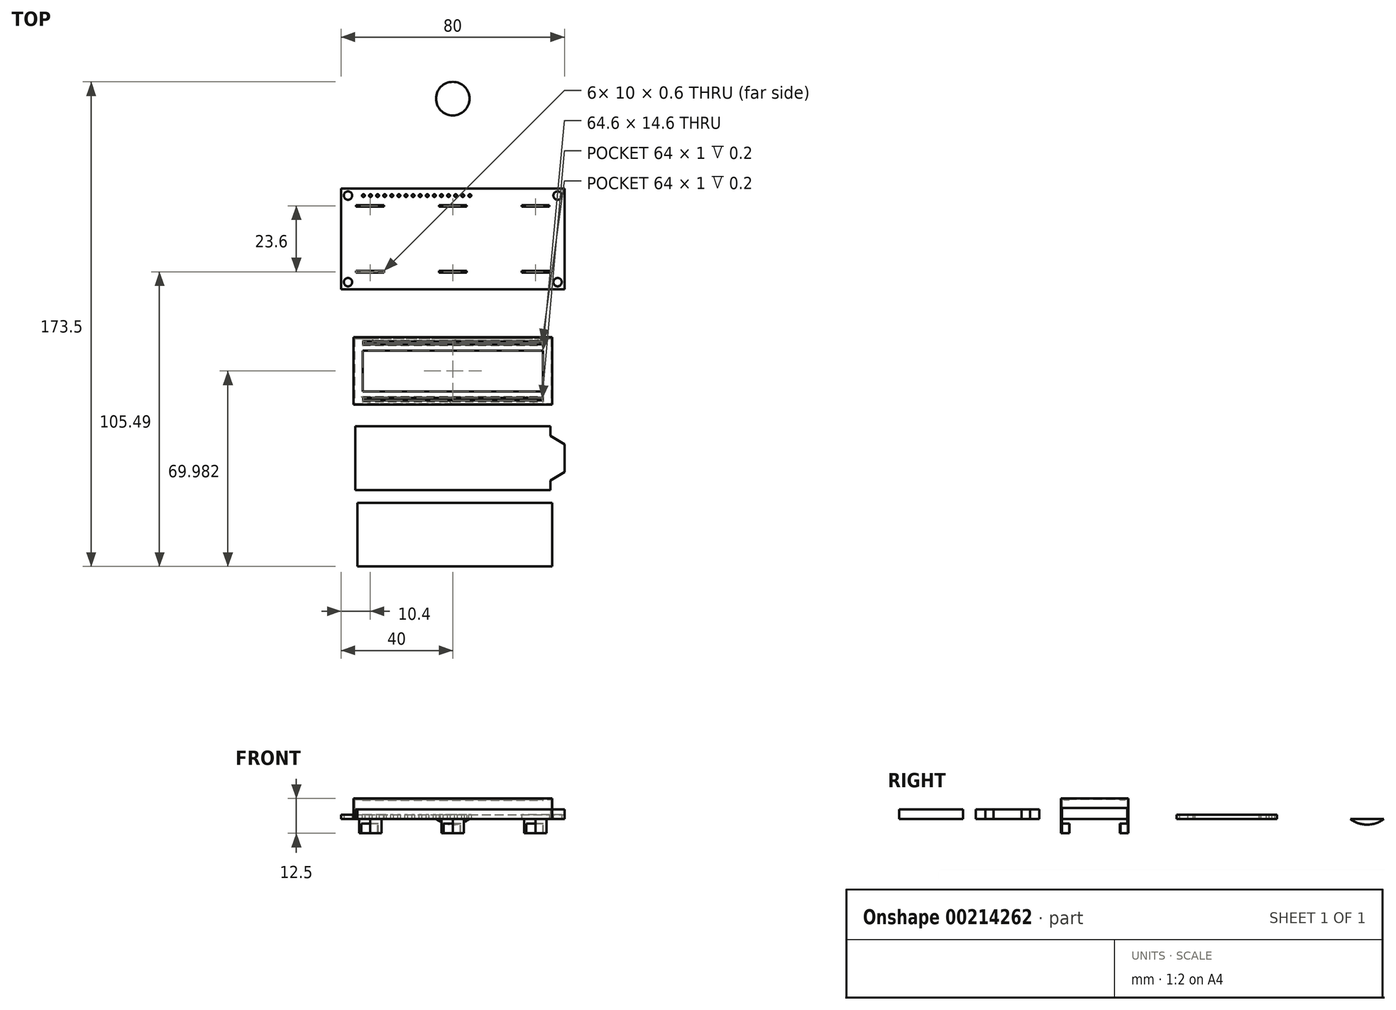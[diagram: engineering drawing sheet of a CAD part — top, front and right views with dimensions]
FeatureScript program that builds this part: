
annotation { "Feature Type Name" : "Feature", "Feature Type Description" : "" }
export const myFeature = defineFeature(function(context is Context, id is Id, definition is map)
    precondition{}
    {
        {
            var Q0;
            Q0=qCreatedBy(makeId("Top.planeOp"),FACE);
            var sketch = newSketch(context, id + "F0", { "sketchPlane" : qUnion([Q0])});
            skLineSegment(sketch, "E0.bottom", {"start": v(-40, 18) * mm, "end": v(40, 18) * mm});
            skLineSegment(sketch, "E0.top", {"start": v(-40, -18) * mm, "end": v(40, -18) * mm});
            skLineSegment(sketch, "E0.left", {"start": v(-40, 18) * mm, "end": v(-40, -18) * mm});
            skLineSegment(sketch, "E0.right", {"start": v(40, 18) * mm, "end": v(40, -18) * mm});
            skSolve(sketch);
        }
        {
            var Q0;
            Q0 = qSketchRegion(id + "F0", true);
            extrude(context, id + "F1", {"entities" : qUnion([Q0]), "depth" : 1.6 * mm});
        }
        {
            var Q0;
            Q0=qCreatedBy(makeId("Top.planeOp"),FACE);
            var sketch = newSketch(context, id + "F2", { "sketchPlane" : qUnion([Q0])});
            skCircle(sketch, "E1", {"center": v(-37.5, 15.5) * mm, "radius": 1.5 * mm});
            skCircle(sketch, "E2", {"center": v(-37.5, -15.5) * mm, "radius": 1.5 * mm});
            skCircle(sketch, "E3", {"center": v(37.5, -15.5) * mm, "radius": 1.5 * mm});
            skCircle(sketch, "E4", {"center": v(37.5, 15.5) * mm, "radius": 1.5 * mm});
            skSolve(sketch);
        }
        {
            var Q0;
            Q0 = qSketchRegion(id + "F2", true);
            extrude(context, id + "F3", {"entities" : qUnion([Q0]), "operationType" : NewBodyOperationType.REMOVE, "endBound" : BoundingType.THROUGH_ALL, "depth" : 25 * mm});
        }
        {
            var Q0;
            Q0=qCreatedBy(makeId("Top.planeOp"),FACE);
            var sketch = newSketch(context, id + "F4", { "sketchPlane" : qUnion([Q0])});
            skCircle(sketch, "E5", {"center": v(-32, 15.5) * mm, "radius": 0.5 * mm});
            skCircle(sketch, "E6.1.0.0", {"center": v(-29.46, 15.5) * mm, "radius": 0.5 * mm});
            skCircle(sketch, "E6.2.0.0", {"center": v(-26.92, 15.5) * mm, "radius": 0.5 * mm});
            skCircle(sketch, "E6.3.0.0", {"center": v(-24.38, 15.5) * mm, "radius": 0.5 * mm});
            skCircle(sketch, "E6.4.0.0", {"center": v(-21.84, 15.5) * mm, "radius": 0.5 * mm});
            skCircle(sketch, "E6.5.0.0", {"center": v(-19.3, 15.5) * mm, "radius": 0.5 * mm});
            skCircle(sketch, "E6.6.0.0", {"center": v(-16.76, 15.5) * mm, "radius": 0.5 * mm});
            skCircle(sketch, "E6.7.0.0", {"center": v(-14.22, 15.5) * mm, "radius": 0.5 * mm});
            skCircle(sketch, "E6.8.0.0", {"center": v(-11.68, 15.5) * mm, "radius": 0.5 * mm});
            skCircle(sketch, "E6.9.0.0", {"center": v(-9.14, 15.5) * mm, "radius": 0.5 * mm});
            skCircle(sketch, "E6.10.0.0", {"center": v(-6.6, 15.5) * mm, "radius": 0.5 * mm});
            skCircle(sketch, "E6.11.0.0", {"center": v(-4.06, 15.5) * mm, "radius": 0.5 * mm});
            skCircle(sketch, "E6.12.0.0", {"center": v(-1.52, 15.5) * mm, "radius": 0.5 * mm});
            skCircle(sketch, "E6.13.0.0", {"center": v(1.02, 15.5) * mm, "radius": 0.5 * mm});
            skCircle(sketch, "E6.14.0.0", {"center": v(3.56, 15.5) * mm, "radius": 0.5 * mm});
            skCircle(sketch, "E6.15.0.0", {"center": v(6.1, 15.5) * mm, "radius": 0.5 * mm});
            skLineSegment(sketch, "E6.direction1", {"start": v(-32, 15.5) * mm, "end": v(-29.46, 15.5) * mm, "construction": true});
            skSolve(sketch);
        }
        {
            var Q0;
            Q0 = qSketchRegion(id + "F4", true);
            extrude(context, id + "F5", {"entities" : qUnion([Q0]), "operationType" : NewBodyOperationType.REMOVE, "endBound" : BoundingType.THROUGH_ALL, "depth" : 25 * mm});
        }
        {
            var Q0;
            Q0=qCreatedBy(makeId("Top.planeOp"),FACE);
            var sketch = newSketch(context, id + "F6", { "sketchPlane" : qUnion([Q0])});
            skLineSegment(sketch, "E7.bottom", {"start": v(-34.6, 12.1) * mm, "end": v(-24.6, 12.1) * mm});
            skLineSegment(sketch, "E7.top", {"start": v(-34.6, 11.5) * mm, "end": v(-24.6, 11.5) * mm});
            skLineSegment(sketch, "E7.left", {"start": v(-34.6, 12.1) * mm, "end": v(-34.6, 11.5) * mm});
            skLineSegment(sketch, "E7.right", {"start": v(-24.6, 12.1) * mm, "end": v(-24.6, 11.5) * mm});
            skLineSegment(sketch, "E8.bottom", {"start": v(-5, 12.1) * mm, "end": v(5, 12.1) * mm});
            skLineSegment(sketch, "E8.top", {"start": v(-5, 11.5) * mm, "end": v(5, 11.5) * mm});
            skLineSegment(sketch, "E8.left", {"start": v(-5, 12.1) * mm, "end": v(-5, 11.5) * mm});
            skLineSegment(sketch, "E8.right", {"start": v(5, 12.1) * mm, "end": v(5, 11.5) * mm});
            skLineSegment(sketch, "E9.bottom", {"start": v(24.6, 12.1) * mm, "end": v(34.6, 12.1) * mm});
            skLineSegment(sketch, "E9.top", {"start": v(24.6, 11.5) * mm, "end": v(34.6, 11.5) * mm});
            skLineSegment(sketch, "E9.left", {"start": v(24.6, 12.1) * mm, "end": v(24.6, 11.5) * mm});
            skLineSegment(sketch, "E9.right", {"start": v(34.6, 12.1) * mm, "end": v(34.6, 11.5) * mm});
            skLineSegment(sketch, "E10.bottom", {"start": v(-34.6, -12.1) * mm, "end": v(-24.6, -12.1) * mm});
            skLineSegment(sketch, "E10.top", {"start": v(-34.6, -11.5) * mm, "end": v(-24.6, -11.5) * mm});
            skLineSegment(sketch, "E10.left", {"start": v(-34.6, -11.5) * mm, "end": v(-34.6, -12.1) * mm});
            skLineSegment(sketch, "E10.right", {"start": v(-24.6, -11.5) * mm, "end": v(-24.6, -12.1) * mm});
            skLineSegment(sketch, "E11.bottom", {"start": v(-5, -12.1) * mm, "end": v(5, -12.1) * mm});
            skLineSegment(sketch, "E11.top", {"start": v(-5, -11.5) * mm, "end": v(5, -11.5) * mm});
            skLineSegment(sketch, "E11.left", {"start": v(-5, -11.5) * mm, "end": v(-5, -12.1) * mm});
            skLineSegment(sketch, "E11.right", {"start": v(5, -11.5) * mm, "end": v(5, -12.1) * mm});
            skLineSegment(sketch, "E12.bottom", {"start": v(24.6, -12.1) * mm, "end": v(34.6, -12.1) * mm});
            skLineSegment(sketch, "E12.top", {"start": v(24.6, -11.5) * mm, "end": v(34.6, -11.5) * mm});
            skLineSegment(sketch, "E12.left", {"start": v(24.6, -11.5) * mm, "end": v(24.6, -12.1) * mm});
            skLineSegment(sketch, "E12.right", {"start": v(34.6, -11.5) * mm, "end": v(34.6, -12.1) * mm});
            skSolve(sketch);
        }
        {
            var Q0;
            Q0 = qSketchRegion(id + "F6", true);
            extrude(context, id + "F7", {"entities" : qUnion([Q0]), "operationType" : NewBodyOperationType.REMOVE, "endBound" : BoundingType.THROUGH_ALL, "depth" : 25 * mm});
        }
        {
            var Q0;
            Q0=qCreatedBy(makeId("Top.planeOp"),FACE);
            var sketch = newSketch(context, id + "F8", { "sketchPlane" : qUnion([Q0])});
            skLineSegment(sketch, "E13.bottom", {"start": v(-35.55, -35.26) * mm, "end": v(35.55, -35.26) * mm});
            skLineSegment(sketch, "E13.top", {"start": v(-35.55, -59.36) * mm, "end": v(35.55, -59.36) * mm});
            skLineSegment(sketch, "E13.left", {"start": v(-35.55, -35.26) * mm, "end": v(-35.55, -59.36) * mm});
            skLineSegment(sketch, "E13.right", {"start": v(35.55, -35.26) * mm, "end": v(35.55, -59.36) * mm});
            skSolve(sketch);
        }
        {
            var Q0;
            Q0 = qSketchRegion(id + "F8", true);
            extrude(context, id + "F9", {"entities" : qUnion([Q0]), "depth" : 7.4 * mm});
        }
        {
            var Q0;
            Q0=makeQuery(id+"F9.opExtrude","CAP_FACE",FACE,{"disambiguationData":[OSD([sQuery(id+"F8.wireOp",EDGE,"E13.bottom"),sQuery(id+"F8.wireOp",EDGE,"E13.top"),sQuery(id+"F8.wireOp",EDGE,"E13.left"),sQuery(id+"F8.wireOp",EDGE,"E13.right")])],"isStart":false});
            var sketch = newSketch(context, id + "F10", { "sketchPlane" : qUnion([Q0])});
            skLineSegment(sketch, "E14.bottom", {"start": v(-32, -36.76) * mm, "end": v(32, -36.76) * mm});
            skLineSegment(sketch, "E14.top", {"start": v(-32, -37.76) * mm, "end": v(32, -37.76) * mm});
            skLineSegment(sketch, "E14.left", {"start": v(-32, -36.76) * mm, "end": v(-32, -37.76) * mm});
            skLineSegment(sketch, "E14.right", {"start": v(32, -36.76) * mm, "end": v(32, -37.76) * mm});
            skLineSegment(sketch, "E15.bottom", {"start": v(-32, -56.86) * mm, "end": v(32, -56.86) * mm});
            skLineSegment(sketch, "E15.top", {"start": v(-32, -57.86) * mm, "end": v(32, -57.86) * mm});
            skLineSegment(sketch, "E15.left", {"start": v(-32, -56.86) * mm, "end": v(-32, -57.86) * mm});
            skLineSegment(sketch, "E15.right", {"start": v(32, -56.86) * mm, "end": v(32, -57.86) * mm});
            skSolve(sketch);
        }
        {
            var Q0;
            Q0 = qSketchRegion(id + "F10", true);
            extrude(context, id + "F11", {"entities" : qUnion([Q0]), "operationType" : NewBodyOperationType.REMOVE, "oppositeDirection" : true, "depth" : .2 * mm});
        }
        {
            var Q0;
            Q0=makeQuery(id+"F9.opExtrude","CAP_FACE",FACE,{"disambiguationData":[OSD([sQuery(id+"F8.wireOp",EDGE,"E13.bottom"),sQuery(id+"F8.wireOp",EDGE,"E13.top"),sQuery(id+"F8.wireOp",EDGE,"E13.left"),sQuery(id+"F8.wireOp",EDGE,"E13.right")])],"isStart":true});
            shell(context, id + "F12", {"entities" : qUnion([Q0]), "thickness" : .4 * mm});
        }
        {
            var Q0;
            Q0=makeQuery(id+"F9.opExtrude","CAP_FACE",FACE,{"disambiguationData":[OSD([sQuery(id+"F8.wireOp",EDGE,"E13.bottom"),sQuery(id+"F8.wireOp",EDGE,"E13.top"),sQuery(id+"F8.wireOp",EDGE,"E13.left"),sQuery(id+"F8.wireOp",EDGE,"E13.right")])],"isStart":false});
            var sketch = newSketch(context, id + "F13", { "sketchPlane" : qUnion([Q0])});
            skLineSegment(sketch, "E16.bottom", {"start": v(-32.3, -40) * mm, "end": v(32.3, -40) * mm});
            skLineSegment(sketch, "E16.top", {"start": v(-32.3, -54.6) * mm, "end": v(32.3, -54.6) * mm});
            skLineSegment(sketch, "E16.left", {"start": v(-32.3, -40) * mm, "end": v(-32.3, -54.6) * mm});
            skLineSegment(sketch, "E16.right", {"start": v(32.3, -40) * mm, "end": v(32.3, -54.6) * mm});
            skSolve(sketch);
        }
        {
            var Q0;
            Q0 = qSketchRegion(id + "F13", true);
            extrude(context, id + "F14", {"entities" : qUnion([Q0]), "operationType" : NewBodyOperationType.REMOVE, "endBound" : BoundingType.THROUGH_ALL, "oppositeDirection" : true, "depth" : 25 * mm});
        }
        {
            var Q0;
            Q0=makeQuery(id+"F9.opExtrude","SWEPT_FACE",FACE,{"disambiguationData":[OSD([sQuery(id+"F8.wireOp",EDGE,"E13.right")])]});
            var sketch = newSketch(context, id + "F15", { "sketchPlane" : qUnion([Q0])});
            skLineSegment(sketch, "E17.bottom", {"start": v(-58.96, 0) * mm, "end": v(-35.66, 0) * mm});
            skLineSegment(sketch, "E17.top", {"start": v(-58.96, 4) * mm, "end": v(-35.66, 4) * mm});
            skLineSegment(sketch, "E17.left", {"start": v(-58.96, 0) * mm, "end": v(-58.96, 4) * mm});
            skLineSegment(sketch, "E17.right", {"start": v(-35.66, 0) * mm, "end": v(-35.66, 4) * mm});
            skSolve(sketch);
        }
        {
            var Q0;
            Q0 = qSketchRegion(id + "F15", true);
            extrude(context, id + "F16", {"entities" : qUnion([Q0]), "operationType" : NewBodyOperationType.REMOVE, "endBound" : BoundingType.UP_TO_NEXT, "oppositeDirection" : true, "depth" : 25 * mm});
        }
        {
            var Q0;
            Q0=makeQuery(id+"F9.opExtrude","CAP_FACE",FACE,{"disambiguationData":[OSD([sQuery(id+"F8.wireOp",EDGE,"E13.bottom"),sQuery(id+"F8.wireOp",EDGE,"E13.top"),sQuery(id+"F8.wireOp",EDGE,"E13.left"),sQuery(id+"F8.wireOp",EDGE,"E13.right")])],"isStart":true});
            var sketch = newSketch(context, id + "F17", { "sketchPlane" : qUnion([Q0])});
            skLineSegment(sketch, "E18.bottom", {"start": v(33.55, 58.96) * mm, "end": v(29.55, 58.96) * mm});
            skLineSegment(sketch, "E18.top", {"start": v(33.55, 59.36) * mm, "end": v(29.55, 59.36) * mm});
            skLineSegment(sketch, "E18.left", {"start": v(33.55, 58.96) * mm, "end": v(33.55, 59.36) * mm});
            skLineSegment(sketch, "E18.right", {"start": v(29.55, 58.96) * mm, "end": v(29.55, 59.36) * mm});
            skLineSegment(sketch, "E19.bottom", {"start": v(0, 35.26) * mm, "end": v(-4, 35.26) * mm});
            skLineSegment(sketch, "E19.top", {"start": v(0, 35.66) * mm, "end": v(-4, 35.66) * mm});
            skLineSegment(sketch, "E19.left", {"start": v(0, 35.26) * mm, "end": v(0, 35.66) * mm});
            skLineSegment(sketch, "E19.right", {"start": v(-4, 35.26) * mm, "end": v(-4, 35.66) * mm});
            skLineSegment(sketch, "E20.bottom", {"start": v(-29.55, 35.26) * mm, "end": v(-33.55, 35.26) * mm});
            skLineSegment(sketch, "E20.top", {"start": v(-29.55, 35.66) * mm, "end": v(-33.55, 35.66) * mm});
            skLineSegment(sketch, "E20.left", {"start": v(-29.55, 35.26) * mm, "end": v(-29.55, 35.66) * mm});
            skLineSegment(sketch, "E20.right", {"start": v(-33.55, 35.26) * mm, "end": v(-33.55, 35.66) * mm});
            skLineSegment(sketch, "E21.bottom", {"start": v(-25.55, 58.96) * mm, "end": v(-29.55, 58.96) * mm});
            skLineSegment(sketch, "E21.top", {"start": v(-25.55, 59.36) * mm, "end": v(-29.55, 59.36) * mm});
            skLineSegment(sketch, "E21.left", {"start": v(-25.55, 58.96) * mm, "end": v(-25.55, 59.36) * mm});
            skLineSegment(sketch, "E21.right", {"start": v(-29.55, 58.96) * mm, "end": v(-29.55, 59.36) * mm});
            skLineSegment(sketch, "E22.bottom", {"start": v(29.55, 35.26) * mm, "end": v(25.55, 35.26) * mm});
            skLineSegment(sketch, "E22.top", {"start": v(29.55, 35.66) * mm, "end": v(25.55, 35.66) * mm});
            skLineSegment(sketch, "E22.left", {"start": v(29.55, 35.26) * mm, "end": v(29.55, 35.66) * mm});
            skLineSegment(sketch, "E22.right", {"start": v(25.55, 35.26) * mm, "end": v(25.55, 35.66) * mm});
            skLineSegment(sketch, "E23.bottom", {"start": v(0, 59.36) * mm, "end": v(4, 59.36) * mm});
            skLineSegment(sketch, "E23.top", {"start": v(0, 58.96) * mm, "end": v(4, 58.96) * mm});
            skLineSegment(sketch, "E23.left", {"start": v(0, 59.36) * mm, "end": v(0, 58.96) * mm});
            skLineSegment(sketch, "E23.right", {"start": v(4, 59.36) * mm, "end": v(4, 58.96) * mm});
            skSolve(sketch);
        }
        {
            var Q0;
            Q0 = qSketchRegion(id + "F17", true);
            extrude(context, id + "F18", {"entities" : qUnion([Q0]), "operationType" : NewBodyOperationType.ADD, "depth" : 1.6 * mm});
        }
        {
            var Q0;
            Q0=makeQuery(id+"F18.opExtrude","CAP_FACE",FACE,{"disambiguationData":[OSD([sQuery(id+"F17.wireOp",EDGE,"E18.bottom"),sQuery(id+"F17.wireOp",EDGE,"E18.top"),sQuery(id+"F17.wireOp",EDGE,"E18.left"),sQuery(id+"F17.wireOp",EDGE,"E18.right")])],"isStart":false});
            var sketch = newSketch(context, id + "F19", { "sketchPlane" : qUnion([Q0])});
            skLineSegment(sketch, "E24", {"start": v(29.55, 58.96) * mm, "end": v(33.55, 58.96) * mm});
            skLineSegment(sketch, "E25", {"start": v(33.55, 58.96) * mm, "end": v(33.55, 59.36) * mm});
            skLineSegment(sketch, "E26", {"start": v(33.55, 59.36) * mm, "end": v(29.55, 59.36) * mm});
            skLineSegment(sketch, "E27", {"start": v(29.55, 59.36) * mm, "end": v(26.31, 56.59) * mm});
            skLineSegment(sketch, "E28", {"start": v(26.31, 56.59) * mm, "end": v(26.51, 56.36) * mm});
            skLineSegment(sketch, "E29", {"start": v(26.51, 56.36) * mm, "end": v(29.55, 58.96) * mm});
            skLineSegment(sketch, "E30.0", {"start": v(0, 58.96) * mm, "end": v(4, 58.96) * mm});
            skLineSegment(sketch, "E31.0", {"start": v(4, 59.36) * mm, "end": v(4, 58.96) * mm});
            skLineSegment(sketch, "E32.0", {"start": v(0, 59.36) * mm, "end": v(4, 59.36) * mm});
            skLineSegment(sketch, "E33", {"start": v(0, 59.36) * mm, "end": v(-3.24, 56.59) * mm});
            skLineSegment(sketch, "E34", {"start": v(-3.24, 56.59) * mm, "end": v(-3.04, 56.36) * mm});
            skLineSegment(sketch, "E35", {"start": v(-3.04, 56.36) * mm, "end": v(0, 58.96) * mm});
            skPoint(sketch, "E36.0", {"position": v(-27.55, 59.36) * mm});
            skLineSegment(sketch, "E37.0", {"start": v(-25.55, 58.96) * mm, "end": v(-25.55, 59.36) * mm});
            skLineSegment(sketch, "E38.0", {"start": v(-29.55, 58.96) * mm, "end": v(-25.55, 58.96) * mm});
            skLineSegment(sketch, "E39.0", {"start": v(-29.55, 59.36) * mm, "end": v(-25.55, 59.36) * mm});
            skLineSegment(sketch, "E40", {"start": v(-29.55, 58.96) * mm, "end": v(-32.59, 56.36) * mm});
            skLineSegment(sketch, "E41", {"start": v(-32.59, 56.36) * mm, "end": v(-32.79, 56.59) * mm});
            skLineSegment(sketch, "E42", {"start": v(-32.79, 56.59) * mm, "end": v(-29.55, 59.36) * mm});
            skLineSegment(sketch, "E43.0", {"start": v(-33.55, 35.26) * mm, "end": v(-29.55, 35.26) * mm});
            skLineSegment(sketch, "E44.0", {"start": v(-33.55, 35.66) * mm, "end": v(-29.55, 35.66) * mm});
            skLineSegment(sketch, "E45.0", {"start": v(-33.55, 35.26) * mm, "end": v(-33.55, 35.66) * mm});
            skLineSegment(sketch, "E46", {"start": v(-29.55, 35.26) * mm, "end": v(-26.69, 38.05) * mm});
            skLineSegment(sketch, "E47", {"start": v(-26.69, 38.05) * mm, "end": v(-26.89, 38.26) * mm});
            skLineSegment(sketch, "E48", {"start": v(-26.89, 38.26) * mm, "end": v(-29.55, 35.66) * mm});
            skLineSegment(sketch, "E49.0", {"start": v(-4, 35.26) * mm, "end": v(0, 35.26) * mm});
            skLineSegment(sketch, "E50.0", {"start": v(-4, 35.26) * mm, "end": v(-4, 35.66) * mm});
            skLineSegment(sketch, "E51.0", {"start": v(-4, 35.66) * mm, "end": v(0, 35.66) * mm});
            skLineSegment(sketch, "E52", {"start": v(0, 35.26) * mm, "end": v(2.86, 38.05) * mm});
            skLineSegment(sketch, "E53", {"start": v(2.86, 38.05) * mm, "end": v(2.66, 38.26) * mm});
            skLineSegment(sketch, "E54", {"start": v(2.66, 38.26) * mm, "end": v(0, 35.66) * mm});
            skLineSegment(sketch, "E55.0", {"start": v(25.55, 35.26) * mm, "end": v(29.55, 35.26) * mm});
            skLineSegment(sketch, "E56.0", {"start": v(25.55, 35.66) * mm, "end": v(29.55, 35.66) * mm});
            skLineSegment(sketch, "E57.0", {"start": v(25.55, 35.26) * mm, "end": v(25.55, 35.66) * mm});
            skLineSegment(sketch, "E58", {"start": v(29.55, 35.26) * mm, "end": v(32.41, 38.05) * mm});
            skLineSegment(sketch, "E59", {"start": v(32.41, 38.05) * mm, "end": v(32.21, 38.26) * mm});
            skLineSegment(sketch, "E60", {"start": v(32.21, 38.26) * mm, "end": v(29.55, 35.66) * mm});
            skSolve(sketch);
        }
        {
            var Q0;
            Q0 = qSketchRegion(id + "F19", true);
            extrude(context, id + "F20", {"entities" : qUnion([Q0]), "operationType" : NewBodyOperationType.ADD, "depth" : 3.5 * mm});
        }
        {
            var Q0;
            Q0=qCreatedBy(makeId("Top.planeOp"),FACE);
            var sketch = newSketch(context, id + "F21", { "sketchPlane" : qUnion([Q0])});
            skLineSegment(sketch, "E61.bottom", {"start": v(-34.9, -67.1) * mm, "end": v(34.9, -67.1) * mm});
            skLineSegment(sketch, "E61.top", {"start": v(-34.9, -89.9) * mm, "end": v(34.9, -89.9) * mm});
            skLineSegment(sketch, "E61.left", {"start": v(-34.9, -67.1) * mm, "end": v(-34.9, -89.9) * mm});
            skLineSegment(sketch, "E61.right", {"start": v(34.9, -67.1) * mm, "end": v(34.9, -70.5) * mm});
            skLineSegment(sketch, "E62", {"start": v(34.9, -70.5) * mm, "end": v(40, -73.5) * mm});
            skLineSegment(sketch, "E63", {"start": v(40, -73.5) * mm, "end": v(40, -83.5) * mm});
            skLineSegment(sketch, "E64", {"start": v(40, -83.5) * mm, "end": v(34.9, -86.5) * mm});
            skLineSegment(sketch, "E65.trimOffspring", {"start": v(34.9, -86.5) * mm, "end": v(34.9, -89.9) * mm});
            skPoint(sketch, "E66", {"position": v(-34.9, -78.5) * mm});
            skPoint(sketch, "E67", {"position": v(40, -78.5) * mm});
            skSolve(sketch);
        }
        {
            var Q0;
            Q0 = qSketchRegion(id + "F21", true);
            extrude(context, id + "F22", {"entities" : qUnion([Q0]), "depth" : 3.5 * mm});
        }
        {
            var Q0;
            Q0=qCreatedBy(makeId("Top.planeOp"),FACE);
            var sketch = newSketch(context, id + "F23", { "sketchPlane" : qUnion([Q0])});
            skLineSegment(sketch, "E68.bottom", {"start": v(-34.17, -94.5) * mm, "end": v(35.63, -94.5) * mm});
            skLineSegment(sketch, "E68.top", {"start": v(-34.17, -117.3) * mm, "end": v(35.63, -117.3) * mm});
            skLineSegment(sketch, "E68.left", {"start": v(-34.17, -94.5) * mm, "end": v(-34.17, -117.3) * mm});
            skLineSegment(sketch, "E68.right", {"start": v(35.63, -94.5) * mm, "end": v(35.63, -117.3) * mm});
            skSolve(sketch);
        }
        {
            var Q0;
            Q0 = qSketchRegion(id + "F23", true);
            extrude(context, id + "F24", {"entities" : qUnion([Q0]), "depth" : 3.5 * mm});
        }
        {
            var Q0;
            Q0=qCreatedBy(makeId("Right.planeOp"),FACE);
            var sketch = newSketch(context, id + "F25", { "sketchPlane" : qUnion([Q0])});
            skLineSegment(sketch, "E69", {"start": v(44.2, 0) * mm, "end": v(50.2, 0) * mm});
            skLineSegment(sketch, "E70", {"start": v(50.2, 0) * mm, "end": v(50.2, -2) * mm});
            skArc(sketch, "E71", {"start": v(44.2, 0) * mm, "mid": v(47.04, -1.49) * mm, "end": v(50.2, -2) * mm});
            skSolve(sketch);
        }
        {
            var Q0;
            Q0 = qSketchRegion(id + "F25", true);
            var Q1;
            Q1=sQuery(id+"F25.wireOp",EDGE,"E70");
            revolve(context, id + "F26", {"entities" : qUnion([Q0]), "axis" : qUnion([Q1]), "revolveType" : RevolveType.FULL});
        }
    });
